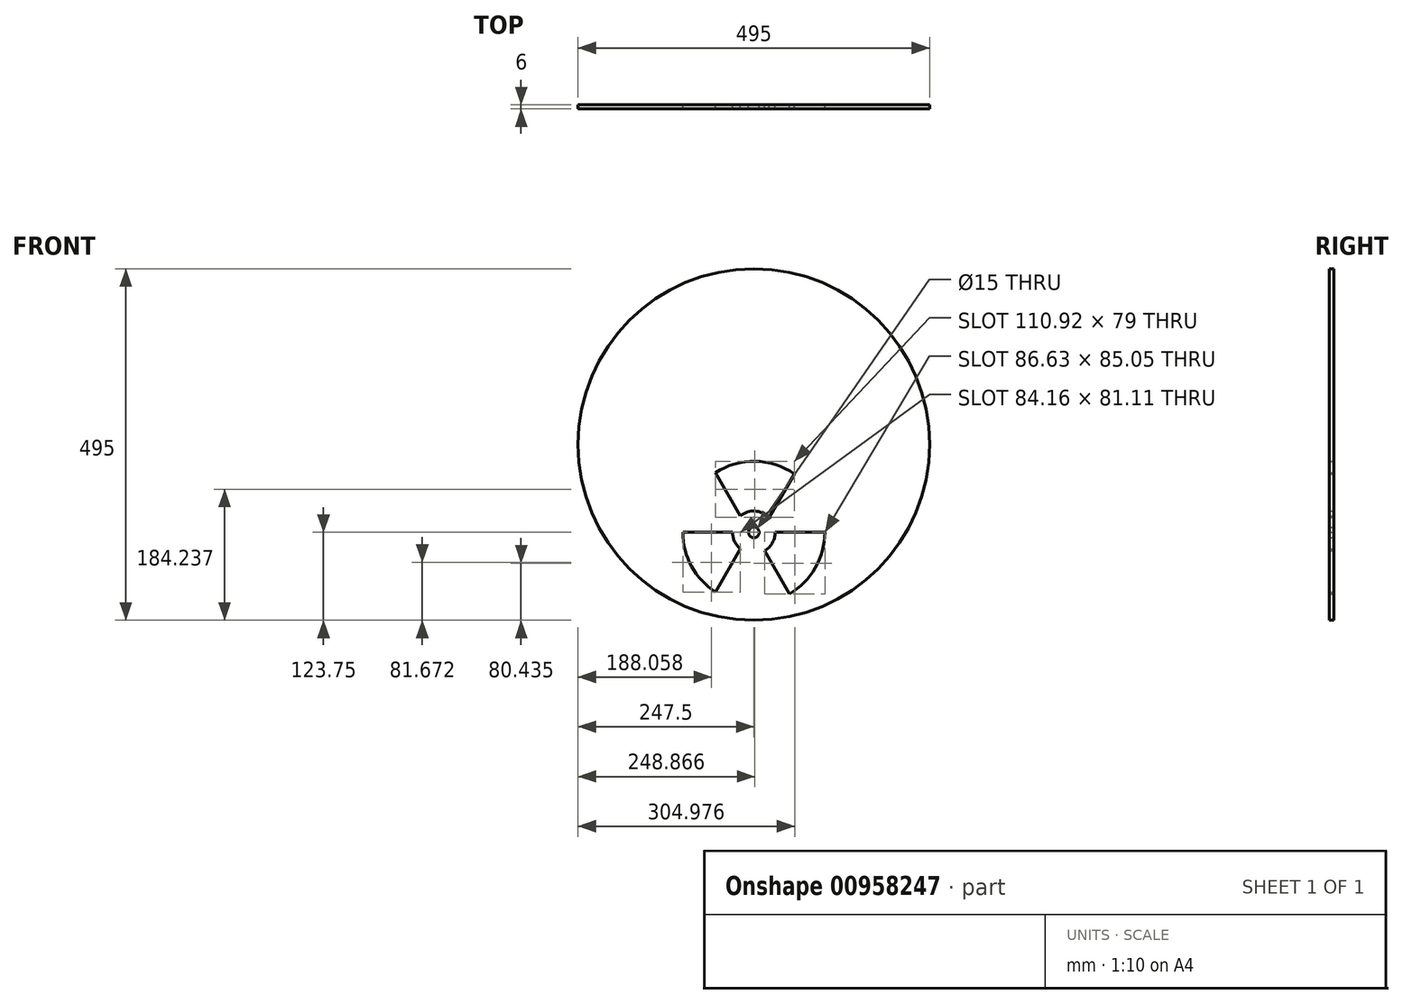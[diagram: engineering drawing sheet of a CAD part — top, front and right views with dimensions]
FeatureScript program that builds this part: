
annotation { "Feature Type Name" : "Feature", "Feature Type Description" : "" }
export const myFeature = defineFeature(function(context is Context, id is Id, definition is map)
    precondition{}
    {
        {
            var Q0;
            Q0=qCreatedBy(makeId("Front.planeOp"),FACE);
            var sketch = newSketch(context, id + "F0", { "sketchPlane" : qUnion([Q0])});
            skCircle(sketch, "E0", {"center": v(0, 0) * mm, "radius": 247.5 * mm});
            skArc(sketch, "E1", {"start": v(-54.1, -39.65) * mm, "mid": v(1.64, -23.76) * mm, "end": v(56.83, -41.47) * mm});
            skArc(sketch, "E2", {"start": v(100, -123.75) * mm, "mid": v(86.59, -173.77) * mm, "end": v(49.95, -210.38) * mm});
            skArc(sketch, "E3", {"start": v(-100, -123.75) * mm, "mid": v(-87.75, -171.7) * mm, "end": v(-54.01, -207.9) * mm});
            skArc(sketch, "E4", {"start": v(-30, -123.75) * mm, "mid": v(-27.08, -136.66) * mm, "end": v(-18.89, -147.06) * mm});
            skArc(sketch, "E5", {"start": v(30, -123.75) * mm, "mid": v(25.97, -138.77) * mm, "end": v(14.95, -149.76) * mm});
            skArc(sketch, "E6", {"start": v(-18.96, -100.5) * mm, "mid": v(1.68, -93.8) * mm, "end": v(21.44, -102.76) * mm});
            skLineSegment(sketch, "E7", {"start": v(-54.1, -39.65) * mm, "end": v(-18.96, -100.5) * mm});
            skLineSegment(sketch, "E8", {"start": v(21.44, -102.76) * mm, "end": v(56.83, -41.47) * mm});
            skLineSegment(sketch, "E9", {"start": v(100, -123.75) * mm, "end": v(30, -123.75) * mm});
            skLineSegment(sketch, "E10", {"start": v(14.95, -149.76) * mm, "end": v(49.95, -210.38) * mm});
            skLineSegment(sketch, "E11", {"start": v(-18.89, -147.06) * mm, "end": v(-54.01, -207.9) * mm});
            skLineSegment(sketch, "E12", {"start": v(-30, -123.75) * mm, "end": v(-100, -123.75) * mm});
            skCircle(sketch, "E13", {"center": v(0, -123.75) * mm, "radius": 7.5 * mm});
            skSolve(sketch);
        }
        {
            var Q0;
            Q0=makeQuery(id+"F0.imprint","IMPRINT",FACE,{"disambiguationData":[TD([[makeQuery(id+"F0.imprint","IMPRINT",EDGE,{"derivedFrom":sQuery(id+"F0.wireOp",EDGE,"E0")}),1.0]])]});
            extrude(context, id + "F1", {"entities" : qUnion([Q0]), "depth" : 6 * mm, "offsetDistance" : 25.4 * mm});
        }
    });
